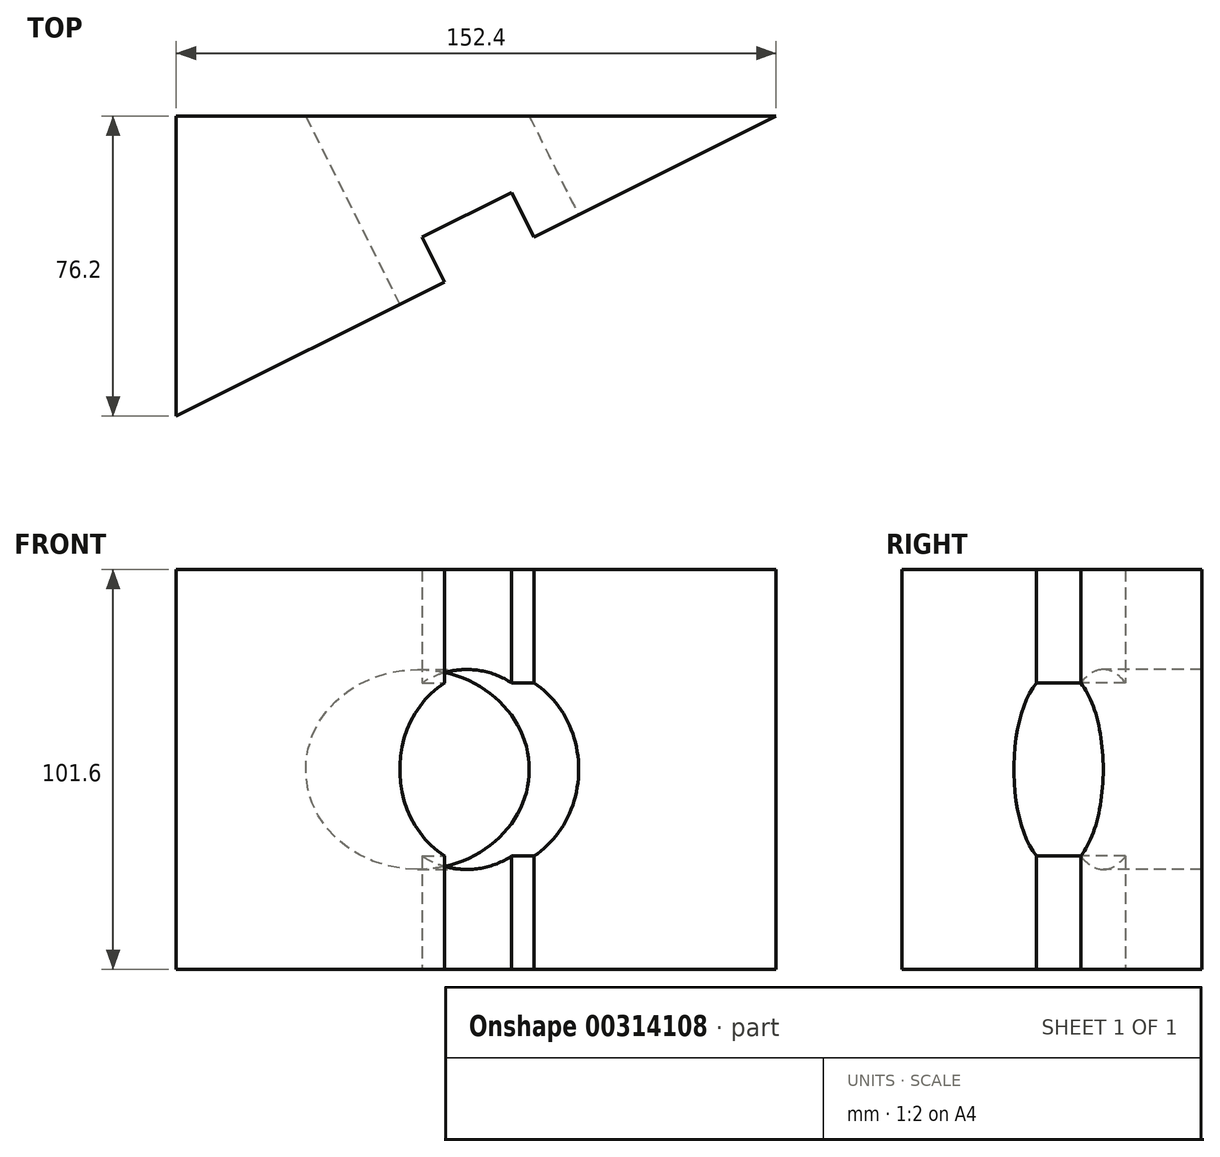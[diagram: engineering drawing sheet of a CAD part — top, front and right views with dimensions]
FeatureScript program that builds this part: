
annotation { "Feature Type Name" : "Feature", "Feature Type Description" : "" }
export const myFeature = defineFeature(function(context is Context, id is Id, definition is map)
    precondition{}
    {
        {
            var Q0;
            Q0=qCreatedBy(makeId("Top.planeOp"),FACE);
            var sketch = newSketch(context, id + "F0", { "sketchPlane" : qUnion([Q0])});
            skLineSegment(sketch, "E0.bottom", {"start": v(0, 0) * mm, "end": v(152.4, 0) * mm});
            skLineSegment(sketch, "E0.top", {"start": v(0, -76.2) * mm, "end": v(152.4, -76.2) * mm});
            skLineSegment(sketch, "E0.left", {"start": v(0, 0) * mm, "end": v(0, -76.2) * mm});
            skLineSegment(sketch, "E0.right", {"start": v(152.4, 0) * mm, "end": v(152.4, -76.2) * mm});
            skLineSegment(sketch, "E1", {"start": v(152.4, 0) * mm, "end": v(0, -76.2) * mm});
            skSolve(sketch);
        }
        {
            var Q0;
            Q0=makeQuery(id+"F0.imprint","IMPRINT",FACE,{"disambiguationData":[TD([[makeQuery(id+"F0.imprint","IMPRINT",EDGE,{"derivedFrom":sQuery(id+"F0.wireOp",EDGE,"E0.bottom")}),-1.0]])]});
            extrude(context, id + "F1", {"entities" : qUnion([Q0]), "depth" : 101.6 * mm});
        }
        {
            var Q0;
            Q0=makeQuery(id+"F1.opExtrude","SWEPT_FACE",FACE,{"disambiguationData":[OSD([sQuery(id+"F0.wireOp",EDGE,"E1")])]});
            var sketch = newSketch(context, id + "F2", { "sketchPlane" : qUnion([Q0])});
            skLineSegment(sketch, "E2.bottom", {"start": v(67.52, 101.6) * mm, "end": v(42.12, 101.6) * mm});
            skLineSegment(sketch, "E2.top", {"start": v(67.52, 0) * mm, "end": v(42.12, 0) * mm});
            skLineSegment(sketch, "E2.left", {"start": v(67.52, 101.6) * mm, "end": v(67.52, 0) * mm});
            skLineSegment(sketch, "E2.right", {"start": v(42.12, 101.6) * mm, "end": v(42.12, 0) * mm});
            skPoint(sketch, "E2.middle", {"position": v(54.82, 50.8) * mm});
            skSolve(sketch);
        }
        {
            var Q0;
            Q0=makeQuery(id+"F2.imprint","IMPRINT",FACE,{"disambiguationData":[TD([[makeQuery(id+"F2.imprint","IMPRINT",EDGE,{"derivedFrom":sQuery(id+"F2.wireOp",EDGE,"E2.bottom")}),1.0]])]});
            extrude(context, id + "F3", {"entities" : qUnion([Q0]), "operationType" : NewBodyOperationType.REMOVE, "oppositeDirection" : true, "depth" : 12.7 * mm});
        }
        {
            var Q0;
            {var subQ0=sQuery(id+"F0.wireOp",EDGE,"E0.bottom");var subQ1=sQuery(id+"F0.wireOp",EDGE,"E1");Q0=makeQuery(id+"F3.boolean.opBoolean","SPLIT",FACE,{"disambiguationData":[TD([makeQuery(id+"F1.opExtrude","SWEPT_FACE",FACE,{"disambiguationData":[OSD([subQ0])]})])],"derivedFrom":makeQuery(id+"F1.opExtrude","SWEPT_FACE",FACE,{"disambiguationData":[OSD([subQ1])]})});}
            var sketch = newSketch(context, id + "F4", { "sketchPlane" : qUnion([Q0])});
            skCircle(sketch, "E3", {"center": v(54.82, 50.8) * mm, "radius": 25.4 * mm});
            skSolve(sketch);
        }
        {
            var Q0;
            {var subQ0=sQuery(id+"F4.wireOp",EDGE,"E3");var subQ1=makeQuery(id+"F3.boolean.opBoolean","COPY",EDGE,{"derivedFrom":makeQuery(id+"F3.opExtrude","CAP_EDGE",EDGE,{"disambiguationData":[OSD([sQuery(id+"F2.wireOp",EDGE,"E2.left")])],"isStart":true})});var subQ2=makeQuery(id+"F4.imprint","INTERSECT",VERTEX,{"disambiguationData":[OD(0.0)],"derivedFrom":[subQ1,subQ0]});Q0=makeQuery(id+"F4.imprint","IMPRINT",FACE,{"disambiguationData":[TD([[makeQuery(id+"F4.imprint","IMPRINT",EDGE,{"disambiguationData":[TD([[subQ2,1.0]])],"derivedFrom":subQ0}),1.0]])]});}
            var Q1;
            {var subQ0=sQuery(id+"F4.wireOp",EDGE,"E3");var subQ1=makeQuery(id+"F3.boolean.opBoolean","COPY",EDGE,{"derivedFrom":makeQuery(id+"F3.opExtrude","CAP_EDGE",EDGE,{"disambiguationData":[OSD([sQuery(id+"F2.wireOp",EDGE,"E2.left")])],"isStart":true})});var subQ2=makeQuery(id+"F4.imprint","INTERSECT",VERTEX,{"disambiguationData":[OD(0.0)],"derivedFrom":[subQ1,subQ0]});Q1=makeQuery(id+"F4.imprint","IMPRINT",FACE,{"disambiguationData":[TD([[makeQuery(id+"F4.imprint","IMPRINT",EDGE,{"disambiguationData":[TD([[subQ2,-1.0]])],"derivedFrom":subQ0}),1.0]])]});}
            extrude(context, id + "F5", {"entities" : qUnion([Q0, Q1]), "operationType" : NewBodyOperationType.REMOVE, "endBound" : BoundingType.THROUGH_ALL, "oppositeDirection" : true, "depth" : 25.4 * mm});
        }
    });
